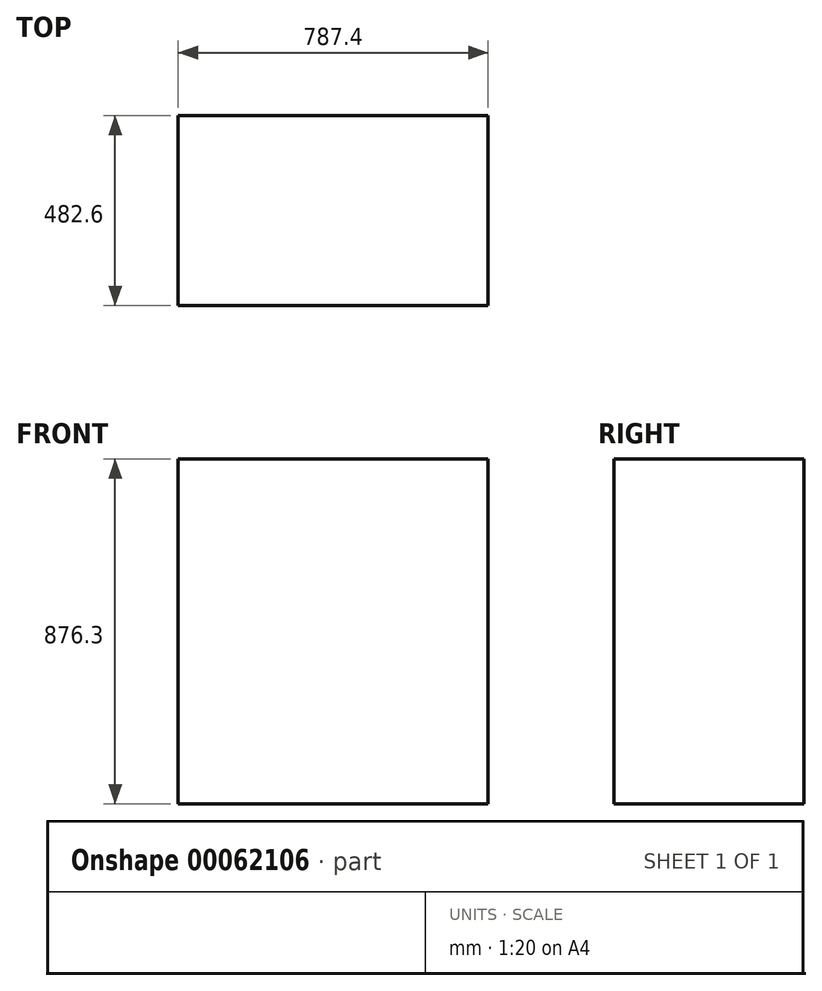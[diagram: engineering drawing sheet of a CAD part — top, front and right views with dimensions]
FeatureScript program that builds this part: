
annotation { "Feature Type Name" : "Feature", "Feature Type Description" : "" }
export const myFeature = defineFeature(function(context is Context, id is Id, definition is map)
    precondition{}
    {
        {
            var Q0;
            Q0=qCreatedBy(makeId("Top.planeOp"),FACE);
            var sketch = newSketch(context, id + "F0", { "sketchPlane" : qUnion([Q0])});
            skLineSegment(sketch, "E0", {"start": v(0, 0) * mm, "end": v(0, 647) * mm, "construction": true});
            skLineSegment(sketch, "E1", {"start": v(0, 0) * mm, "end": v(779.22, 0) * mm, "construction": true});
            skLineSegment(sketch, "E2.bottom", {"start": v(-393.7, 241.3) * mm, "end": v(393.7, 241.3) * mm});
            skLineSegment(sketch, "E2.top", {"start": v(-393.7, -241.3) * mm, "end": v(393.7, -241.3) * mm});
            skLineSegment(sketch, "E2.left", {"start": v(-393.7, 241.3) * mm, "end": v(-393.7, -241.3) * mm});
            skLineSegment(sketch, "E2.right", {"start": v(393.7, 241.3) * mm, "end": v(393.7, -241.3) * mm});
            skSolve(sketch);
        }
        {
            var Q0;
            Q0=makeQuery(id+"F0.imprint","IMPRINT",FACE,{"disambiguationData":[TD([[makeQuery(id+"F0.imprint","IMPRINT",EDGE,{"derivedFrom":sQuery(id+"F0.wireOp",EDGE,"E2.bottom")}),-1.0]])]});
            extrude(context, id + "F1", {"entities" : qUnion([Q0]), "depth" : 876.3 * mm});
        }
    });
